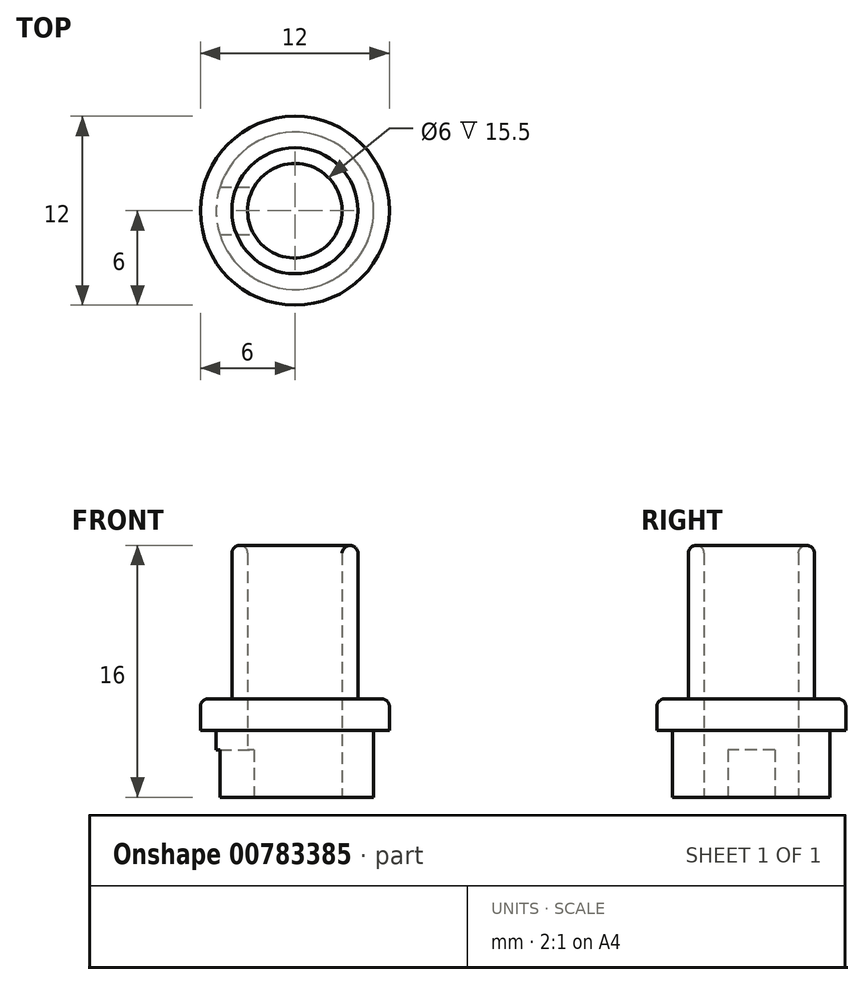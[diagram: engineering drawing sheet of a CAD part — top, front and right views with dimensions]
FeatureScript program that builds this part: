
annotation { "Feature Type Name" : "Feature", "Feature Type Description" : "" }
export const myFeature = defineFeature(function(context is Context, id is Id, definition is map)
    precondition{}
    {
        {
            var Q0;
            Q0=qCreatedBy(makeId("Top.planeOp"),FACE);
            var sketch = newSketch(context, id + "F0", { "sketchPlane" : qUnion([Q0])});
            skCircle(sketch, "E0", {"center": v(0, 0) * mm, "radius": 5 * mm});
            skCircle(sketch, "E1", {"center": v(0, 0) * mm, "radius": 4 * mm});
            skCircle(sketch, "E2", {"center": v(0, 0) * mm, "radius": 6 * mm});
            skSolve(sketch);
        }
        {
            var Q0;
            Q0=makeQuery(id+"F0.imprint","IMPRINT",FACE,{"disambiguationData":[TD([[makeQuery(id+"F0.imprint","IMPRINT",EDGE,{"derivedFrom":sQuery(id+"F0.wireOp",EDGE,"E1")}),1.0]])]});
            extrude(context, id + "F1", {"entities" : qUnion([Q0]), "depth" : 16 * mm, "offsetDistance" : 25 * mm});
        }
        {
            var Q0;
            Q0=makeQuery(id+"F0.imprint","IMPRINT",FACE,{"disambiguationData":[TD([[makeQuery(id+"F0.imprint","IMPRINT",EDGE,{"derivedFrom":sQuery(id+"F0.wireOp",EDGE,"E0")}),1.0]])]});
            extrude(context, id + "F2", {"entities" : qUnion([Q0]), "operationType" : NewBodyOperationType.ADD, "depth" : 6.25 * mm, "offsetDistance" : 25 * mm});
        }
        {
            var Q0;
            Q0=sQuery(id+"F0.wireOp",VERTEX,"E0.center");
            var Q1;
            Q1=makeQuery(id+"F1.opExtrude","SWEPT_BODY",BODY,{"disambiguationData":[OSD([sQuery(id+"F0.wireOp",EDGE,"E1")])]});
            hole(context, id + "F3", {"style" : HoleStyle.SIMPLE, "endStyle" : HoleEndStyle.THROUGH, "oppositeDirection" : true, "holeDiameter" : 6 * mm, "majorDiameter" : 5 * mm, "isTappedThrough" : true, "tappedDepth" : 12 * mm, "tapClearance" : 3, "locations" : qUnion([Q0]), "scope" : qUnion([Q1])});
        }
        {
            var Q0;
            Q0=makeQuery(id+"F0.imprint","IMPRINT",FACE,{"disambiguationData":[TD([[makeQuery(id+"F0.imprint","IMPRINT",EDGE,{"derivedFrom":sQuery(id+"F0.wireOp",EDGE,"E0")}),-1.0]])]});
            extrude(context, id + "F4", {"entities" : qUnion([Q0]), "operationType" : NewBodyOperationType.ADD, "depth" : 6.25 * mm, "offsetDistance" : 25 * mm});
        }
        {
            var Q0;
            Q0=makeQuery(id+"F0.imprint","IMPRINT",FACE,{"disambiguationData":[TD([[makeQuery(id+"F0.imprint","IMPRINT",EDGE,{"derivedFrom":sQuery(id+"F0.wireOp",EDGE,"E0")}),-1.0]])]});
            extrude(context, id + "F5", {"entities" : qUnion([Q0]), "operationType" : NewBodyOperationType.REMOVE, "depth" : 4.25 * mm, "offsetDistance" : 25 * mm});
        }
        {
            var Q0;
            Q0=qCreatedBy(makeId("Right.planeOp"),FACE);
            var sketch = newSketch(context, id + "F6", { "sketchPlane" : qUnion([Q0])});
            skLineSegment(sketch, "E3", {"start": v(0, 0) * mm, "end": v(1.5, 0) * mm});
            skLineSegment(sketch, "E4", {"start": v(1.5, 0) * mm, "end": v(1.5, 3) * mm});
            skLineSegment(sketch, "E5", {"start": v(1.5, 3) * mm, "end": v(-1.5, 3) * mm});
            skLineSegment(sketch, "E6", {"start": v(-1.5, 3) * mm, "end": v(-1.5, 0) * mm});
            skLineSegment(sketch, "E7", {"start": v(-1.5, 0) * mm, "end": v(0, 0) * mm});
            skSolve(sketch);
        }
        {
            var Q0;
            Q0=makeQuery(id+"F6.imprint","IMPRINT",FACE,{"disambiguationData":[TD([[makeQuery(id+"F6.imprint","IMPRINT",EDGE,{"derivedFrom":sQuery(id+"F6.wireOp",EDGE,"E3")}),1.0]])]});
            extrude(context, id + "F7", {"entities" : qUnion([Q0]), "operationType" : NewBodyOperationType.REMOVE, "oppositeDirection" : true, "depth" : 25 * mm, "offsetDistance" : 25 * mm});
        }
        {
            var Q0;
            Q0=makeQuery(id+"F1.opExtrude","CAP_FACE",FACE,{"disambiguationData":[OSD([sQuery(id+"F0.wireOp",EDGE,"E1")])],"isStart":false});
            var Q1;
            Q1=makeQuery(id+"F4.opExtrude","CAP_EDGE",EDGE,{"disambiguationData":[OSD([sQuery(id+"F0.wireOp",EDGE,"E2")])],"isStart":false});
            var Q2;
            Q2=makeQuery(id+"F3.hole-0.boolean.opBoolean","COPY",EDGE,{"derivedFrom":makeQuery(id+"F3.hole-0.opRevolve","SWEPT_EDGE",EDGE,{"disambiguationData":[OSD([sQuery(id+"F3.hole-0.sketch.wireOp",EDGE,"core_line_2"),sQuery(id+"F3.hole-0.sketch.wireOp",EDGE,"core_line_3")])]})});
            var Q3;
            Q3=makeQuery(id+"F7.boolean.opBoolean","INTERSECT",EDGE,{"derivedFrom":[makeQuery(id+"F3.hole-0.boolean.opBoolean","COPY",FACE,{"derivedFrom":makeQuery(id+"F3.hole-0.opRevolve","SWEPT_FACE",FACE,{"disambiguationData":[OSD([sQuery(id+"F3.hole-0.sketch.wireOp",EDGE,"core_line_2")])]})}),makeQuery(id+"F7.opExtrude","SWEPT_FACE",FACE,{"disambiguationData":[OSD([sQuery(id+"F6.wireOp",EDGE,"E6")])]})]});
            var Q4;
            Q4=makeQuery(id+"F7.boolean.opBoolean","INTERSECT",EDGE,{"derivedFrom":[makeQuery(id+"F3.hole-0.boolean.opBoolean","COPY",FACE,{"derivedFrom":makeQuery(id+"F3.hole-0.opRevolve","SWEPT_FACE",FACE,{"disambiguationData":[OSD([sQuery(id+"F3.hole-0.sketch.wireOp",EDGE,"core_line_2")])]})}),makeQuery(id+"F7.opExtrude","SWEPT_FACE",FACE,{"disambiguationData":[OSD([sQuery(id+"F6.wireOp",EDGE,"E4")])]})]});
            var Q5;
            Q5=makeQuery(id+"F7.boolean.opBoolean","INTERSECT",EDGE,{"derivedFrom":[makeQuery(id+"F3.hole-0.boolean.opBoolean","COPY",FACE,{"derivedFrom":makeQuery(id+"F3.hole-0.opRevolve","SWEPT_FACE",FACE,{"disambiguationData":[OSD([sQuery(id+"F3.hole-0.sketch.wireOp",EDGE,"core_line_2")])]})}),makeQuery(id+"F7.opExtrude","SWEPT_FACE",FACE,{"disambiguationData":[OSD([sQuery(id+"F6.wireOp",EDGE,"E5")])]})]});
            var Q6;
            Q6=makeQuery(id+"F7.boolean.opBoolean","COPY",EDGE,{"derivedFrom":makeQuery(id+"F7.opExtrude","SWEPT_EDGE",EDGE,{"disambiguationData":[OSD([sQuery(id+"F6.wireOp",EDGE,"E3"),sQuery(id+"F6.wireOp",EDGE,"E4")])]})});
            var Q7;
            Q7=makeQuery(id+"F7.boolean.opBoolean","COPY",EDGE,{"derivedFrom":makeQuery(id+"F7.opExtrude","SWEPT_EDGE",EDGE,{"disambiguationData":[OSD([sQuery(id+"F6.wireOp",EDGE,"E6"),sQuery(id+"F6.wireOp",EDGE,"E7")])]})});
            fillet(context, id + "F8", {"entities" : qUnion([Q0, Q1, Q2, Q3, Q4, Q5, Q6, Q7]), "radius" : 0.5 * mm, "tangentPropagation" : true, "allowEdgeOverflow" : false});
        }
    });
